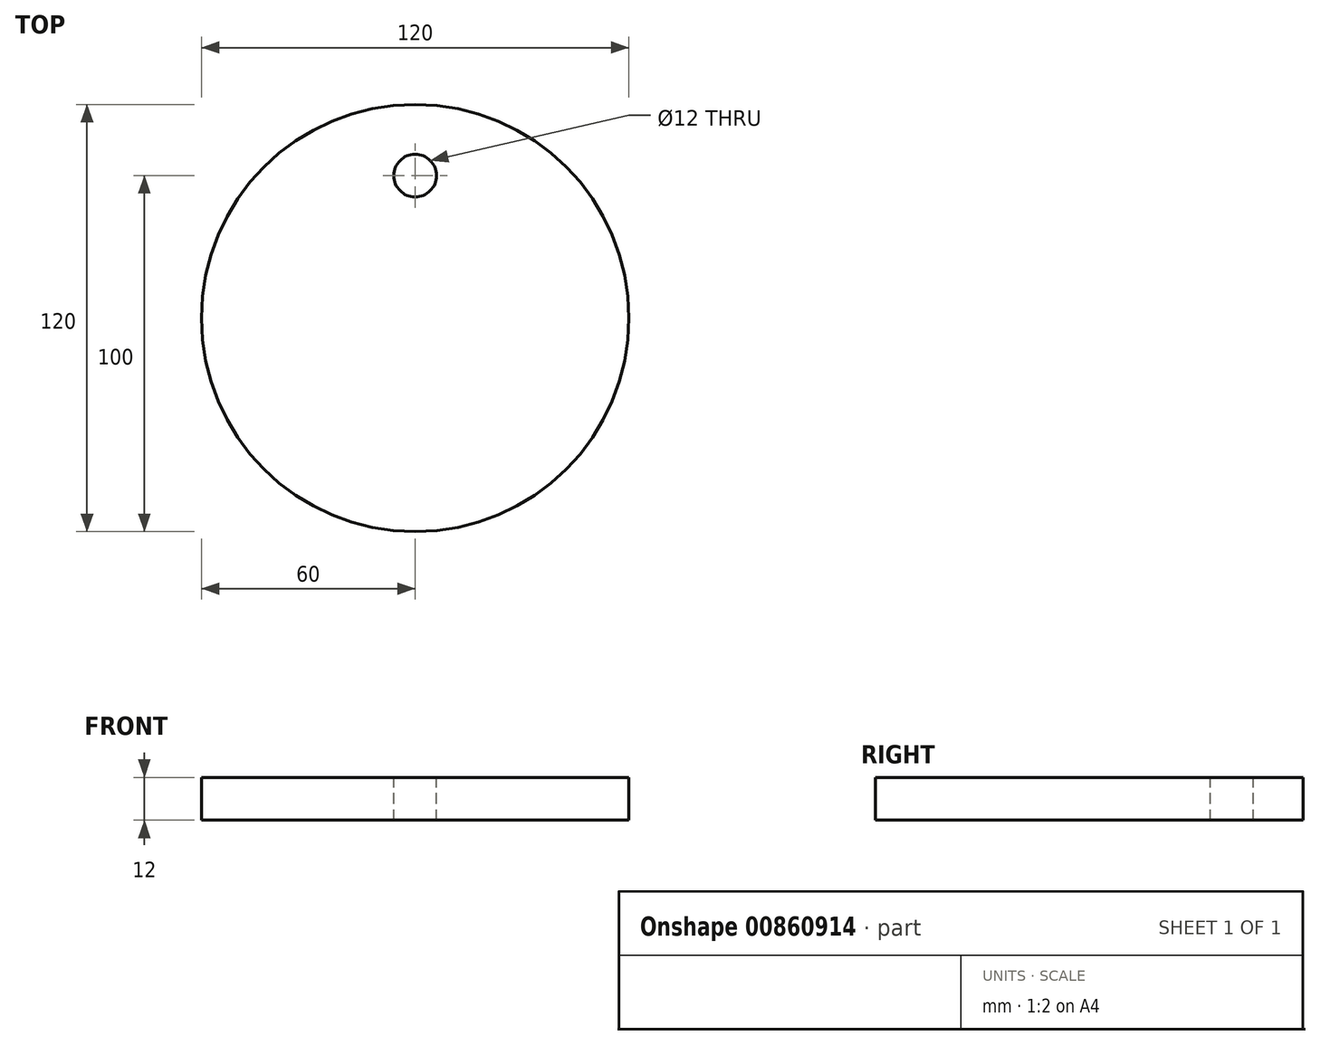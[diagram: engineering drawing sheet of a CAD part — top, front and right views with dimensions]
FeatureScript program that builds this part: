
annotation { "Feature Type Name" : "Feature", "Feature Type Description" : "" }
export const myFeature = defineFeature(function(context is Context, id is Id, definition is map)
    precondition{}
    {
        {
            assignVariable(context, id + "F0", {"name" : "bigcircle", "anyValue" : 120});
        }
        {
            assignVariable(context, id + "F1", {"name" : "thickness", "anyValue" : getVariable(context, 'bigcircle') / 10});
        }
        {
            var Q0;
            Q0=qCreatedBy(makeId("Top.planeOp"),FACE);
            var sketch = newSketch(context, id + "F2", { "sketchPlane" : qUnion([Q0])});
            skCircle(sketch, "E0", {"center": v(0, 0) * mm, "radius": 60 * mm});
            skSolve(sketch);
        }
        {
            var Q0;
            Q0=makeQuery(id+"F2.imprint","IMPRINT",FACE,{"disambiguationData":[TD([[makeQuery(id+"F2.imprint","IMPRINT",EDGE,{"derivedFrom":sQuery(id+"F2.wireOp",EDGE,"E0")}),1.0]])]});
            extrude(context, id + "F3", {"entities" : qUnion([Q0]), "oppositeDirection" : true, "depth" : (getVariable(context, 'thickness')) * mm, "offsetDistance" : 25 * mm});
        }
        {
            var Q0;
            Q0=makeQuery(id+"F3.opExtrude","CAP_FACE",FACE,{"disambiguationData":[OSD([sQuery(id+"F2.wireOp",EDGE,"E0")])],"isStart":true});
            var sketch = newSketch(context, id + "F4", { "sketchPlane" : qUnion([Q0])});
            skCircle(sketch, "E1", {"center": v(0, 0) * mm, "radius": 40 * mm, "construction": true});
            skCircle(sketch, "E2", {"center": v(0, 40) * mm, "radius": 6 * mm});
            skSolve(sketch);
        }
        {
            var Q0;
            Q0=makeQuery(id+"F4.imprint","IMPRINT",FACE,{"disambiguationData":[TD([[makeQuery(id+"F4.imprint","IMPRINT",EDGE,{"derivedFrom":sQuery(id+"F4.wireOp",EDGE,"E2")}),1.0]])]});
            extrude(context, id + "F5", {"entities" : qUnion([Q0]), "operationType" : NewBodyOperationType.REMOVE, "endBound" : BoundingType.THROUGH_ALL, "oppositeDirection" : true, "depth" : 25 * mm, "offsetDistance" : 25 * mm});
        }
    });
